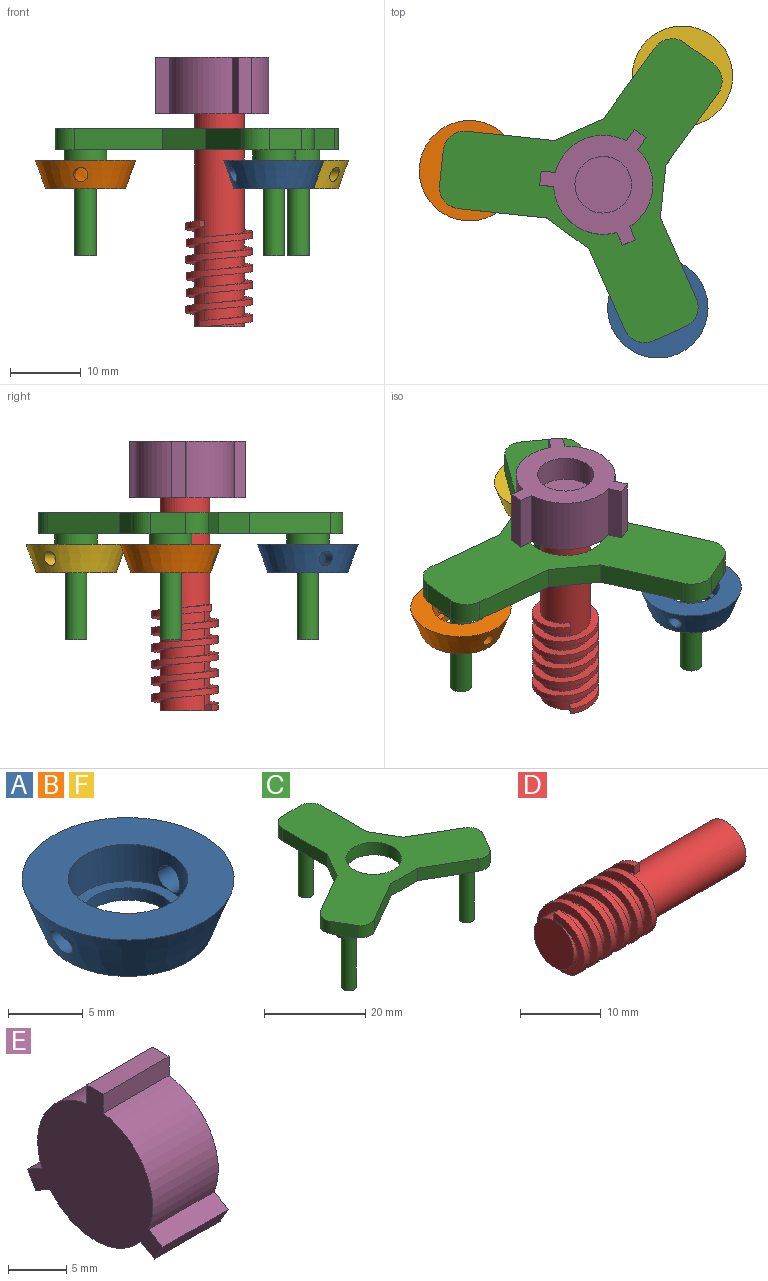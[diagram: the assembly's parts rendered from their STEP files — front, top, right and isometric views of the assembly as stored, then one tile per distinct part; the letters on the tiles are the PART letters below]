
ASSEMBLY  parts=6 mates=3
PART A: 8 faces, bbox 14.2x14.2x4 mm
  f0: cone r=7.09mm half-angle=20deg, axis (0,0,1), area 163.5mm2, adj f2,f3,f6,f7
  f1: cylinder r=4mm len=8mm, axis (0,0,1), area 69.1mm2, adj f3,f4,f6,f7
  f2: plane 11.27x11.27mm, normal (0,0,-1), area 67.6mm2, adj f0,f5
  f3: plane 14.18x14.18mm, normal (0,0,1), area 107.7mm2, adj f0,f1
  f4: plane 8x8mm, normal (0,0,1), area 18.1mm2, adj f1,f5
  f5: cylinder r=3.2mm len=6.4mm, axis (0,0,1), area 20.1mm2, adj f2,f4
  f6: cylinder r=1mm len=2.86mm, axis (-1,0,0), area 15mm2, adj f0,f1
  f7: cylinder r=1mm len=2.86mm, axis (-1,0,0), area 15mm2, adj f0,f1
PART B: same geometry as A
PART C: 33 faces, bbox 43.1x38.2x18 mm
  f0: plane 43.14x38.17mm, normal (0,0,-1), area 539.2mm2, adj f1,f2,f3,f4,f5,f6,f7,f8
  f1: plane 5x3mm, normal (0,1,0), area 15mm2, adj f0,f14,f27,f32
  f2: plane 12.53x3mm, normal (1,0,0), area 37.6mm2, adj f0,f3,f14,f27
  f3: plane 6.45x3.72mm, normal (0.87,0.5,0), area 22.3mm2, adj f0,f2,f4,f14
  f4: plane 10.85x6.26mm, normal (0.5,0.87,0), area 37.6mm2, adj f0,f3,f14,f28
  f5: plane 4.33x3mm, normal (0.87,-0.5,0), area 15mm2, adj f0,f14,f28,f29
  f6: plane 10.85x6.26mm, normal (-0.5,-0.87,0), area 37.6mm2, adj f0,f7,f14,f29
  f7: plane 7.45x3mm, normal (0,-1,0), area 22.3mm2, adj f0,f6,f8,f14
  f8: plane 10.85x6.26mm, normal (0.5,-0.87,0), area 37.6mm2, adj f0,f7,f14,f30
  f9: plane 4.33x3mm, normal (-0.87,-0.5,0), area 15mm2, adj f0,f14,f30,f31
  f10: plane 10.85x6.26mm, normal (-0.5,0.87,0), area 37.6mm2, adj f0,f11,f14,f31
  f11: plane 6.45x3.72mm, normal (-0.87,0.5,0), area 22.3mm2, adj f0,f10,f13,f14
  f12: cylinder r=5.5mm len=11mm, axis (0,0,1), area 103.7mm2, adj f0,f14
  f13: plane 12.53x3mm, normal (-1,0,0), area 37.6mm2, adj f0,f11,f14,f32
  f14: plane 43.14x38.17mm, normal (0,0,1), area 624mm2, adj f1,f2,f3,f4,f5,f6,f7,f8
  f15: cylinder r=1.5mm len=13.5mm, axis (0,0,1), area 127.2mm2, adj f16,f18
  f16: plane 6x6mm, normal (0,0,-1), area 21.2mm2, adj f15,f17
  f17: cylinder r=3mm len=6mm, axis (0,0,1), area 28.3mm2, adj f0,f16
  f18: plane 3x3mm, normal (0,0,-1), area 7.1mm2, adj f15
  f19: cylinder r=1.5mm len=13.5mm, axis (0,0,1), area 127.2mm2, adj f20,f22
  f20: plane 6x6mm, normal (0,0,-1), area 21.2mm2, adj f19,f21
  f21: cylinder r=3mm len=6mm, axis (0,0,1), area 28.3mm2, adj f0,f20
  f22: plane 3x3mm, normal (0,0,-1), area 7.1mm2, adj f19
  f23: cylinder r=1.5mm len=13.5mm, axis (0,0,1), area 127.2mm2, adj f24,f26
  f24: plane 6x6mm, normal (0,0,-1), area 21.2mm2, adj f23,f25
  f25: cylinder r=3mm len=6mm, axis (0,0,1), area 28.3mm2, adj f0,f24
  f26: plane 3x3mm, normal (0,0,-1), area 7.1mm2, adj f23
  f27: cylinder r=3mm len=3mm, axis (0,0,1), area 14.1mm2, adj f0,f1,f2,f14
  f28: cylinder r=3mm len=4.1mm, axis (0,0,1), area 14.1mm2, adj f0,f4,f5,f14
  f29: cylinder r=3mm len=4.1mm, axis (0,0,1), area 14.1mm2, adj f0,f5,f6,f14
  f30: cylinder r=3mm len=4.1mm, axis (0,0,1), area 14.1mm2, adj f0,f8,f9,f14
  f31: cylinder r=3mm len=4.1mm, axis (0,0,1), area 14.1mm2, adj f0,f9,f10,f14
  f32: cylinder r=3mm len=3mm, axis (0,0,1), area 14.1mm2, adj f0,f1,f13,f14
PART D: 14 faces, bbox 30.1x10.9x9.4 mm
  f0: cylinder r=3.5mm len=7mm, axis (-1,0,0), area 32.5mm2, adj f1,f6,f10,f11
  f1: cylinder r=3.5mm len=7mm, axis (-1,0,0), area 32.5mm2, adj f0,f2,f10,f11
  f2: cylinder r=3.5mm len=7mm, axis (-1,0,0), area 32.5mm2, adj f1,f3,f10,f11
  f3: cylinder r=3.5mm len=7mm, axis (-1,0,0), area 32.5mm2, adj f2,f4,f10,f11
  f4: cylinder r=3.5mm len=7mm, axis (-1,0,0), area 32.5mm2, adj f3,f5,f10,f11
  f5: cylinder r=3.5mm len=17.48mm, axis (-1,0,0), area 358.5mm2, adj f4,f9,f11,f13
  f6: cylinder r=3.5mm len=7mm, axis (-1,0,0), area 25.9mm2, adj f0,f7,f8,f10
  f7: plane 7x7mm, normal (-1,0,0), area 38.5mm2, adj f6
  f8: plane 1.2x0.88mm, normal (0,1,0), area 1.1mm2, adj f6,f10,f11,f12
  f9: plane 1.2x0.88mm, normal (0,-1,0), area 1.1mm2, adj f5,f10,f11,f12
  f10: bspline ~14.12x10.85mm, area 186.3mm2, adj f0,f1,f2,f3,f4,f6,f8,f9
  f11: bspline ~14.12x10.85mm, area 186.1mm2, adj f0,f1,f2,f3,f4,f5,f8,f9
  f12: cylinder r=4.7mm len=15mm, axis (1,0,0), area 155.4mm2, adj f8,f9,f10,f11
  f13: plane 7x7mm, normal (1,0,0), area 38.5mm2, adj f5
PART E: 16 faces, bbox 8x16.5x15.9 mm
  f0: plane 8x1.73mm, normal (0,0.5,0.87), area 16mm2, adj f1,f11,f12,f13
  f1: cylinder r=7mm len=9.53mm, axis (-1,0,0), area 101.2mm2, adj f0,f2,f12,f13
  f2: plane 8x2mm, normal (0,1,0), area 16mm2, adj f1,f3,f12,f13
  f3: plane 8x2mm, normal (0,0,1), area 16mm2, adj f2,f4,f12,f13
  f4: plane 8x2mm, normal (0,-1,0), area 16mm2, adj f3,f5,f12,f13
  f5: cylinder r=7mm len=9.53mm, axis (-1,0,0), area 101.2mm2, adj f4,f6,f12,f13
  f6: plane 8x1.73mm, normal (0,-0.5,0.87), area 16mm2, adj f5,f7,f12,f13
  f7: plane 8x1.73mm, normal (0,-0.87,-0.5), area 16mm2, adj f6,f8,f12,f13
  f8: plane 8x1.73mm, normal (0,0.5,-0.87), area 16mm2, adj f7,f9,f12,f13
  f9: cylinder r=7mm len=11mm, axis (-1,0,0), area 101.2mm2, adj f8,f10,f12,f13
  f10: plane 8x1.73mm, normal (0,-0.5,-0.87), area 16mm2, adj f9,f11,f12,f13
  f11: plane 8x1.73mm, normal (0,0.87,-0.5), area 16mm2, adj f0,f10,f12,f13
  f12: plane 16.46x15.93mm, normal (1,0,0), area 115.4mm2, adj f0,f1,f2,f3,f4,f5,f6,f7
  f13: plane 16.46x15.93mm, normal (-1,0,0), area 165.7mm2, adj f0,f1,f2,f3,f4,f5,f6,f7
  f14: cylinder r=4mm len=8mm, axis (1,0,0), area 90.5mm2, adj f12,f15
  f15: plane 8x8mm, normal (1,0,0), area 50.3mm2, adj f14
PART F: same geometry as A
PLACE A rot(axis=(0,0,-1),156.1deg) t=(-2.12,-10.16,61.49)mm
PLACE B rot(axis=(0,0,1),83.9deg) t=(-2.12,-10.16,61.49)mm
PLACE C rot(axis=(0,0,-1),36.1deg) t=(-2.12,-10.16,62.99)mm
PLACE D rot(axis=(0.41,-0.81,0.41),101.9deg) t=(-2.12,-10.16,64.83)mm
PLACE E rot(axis=(-0.67,-0.34,-0.67),142.6deg) t=(-2.12,-10.16,76.83)mm
PLACE F rot(axis=(0,0,-1),36.1deg) t=(-2.12,-10.16,61.49)mm
MATE cylindrical D.f12 <-> C.f12  axis (0,0,1) through (-2.12,-10.16,80.83)mm
MATE revolute F.f0 <-> C.f15  axis (0,0,-1) through (9.06,5.2,74.24)mm
MATE cylindrical E.f9 <-> D.f12  axis (0,0,1) through (-2.12,-10.16,80.83)mm
